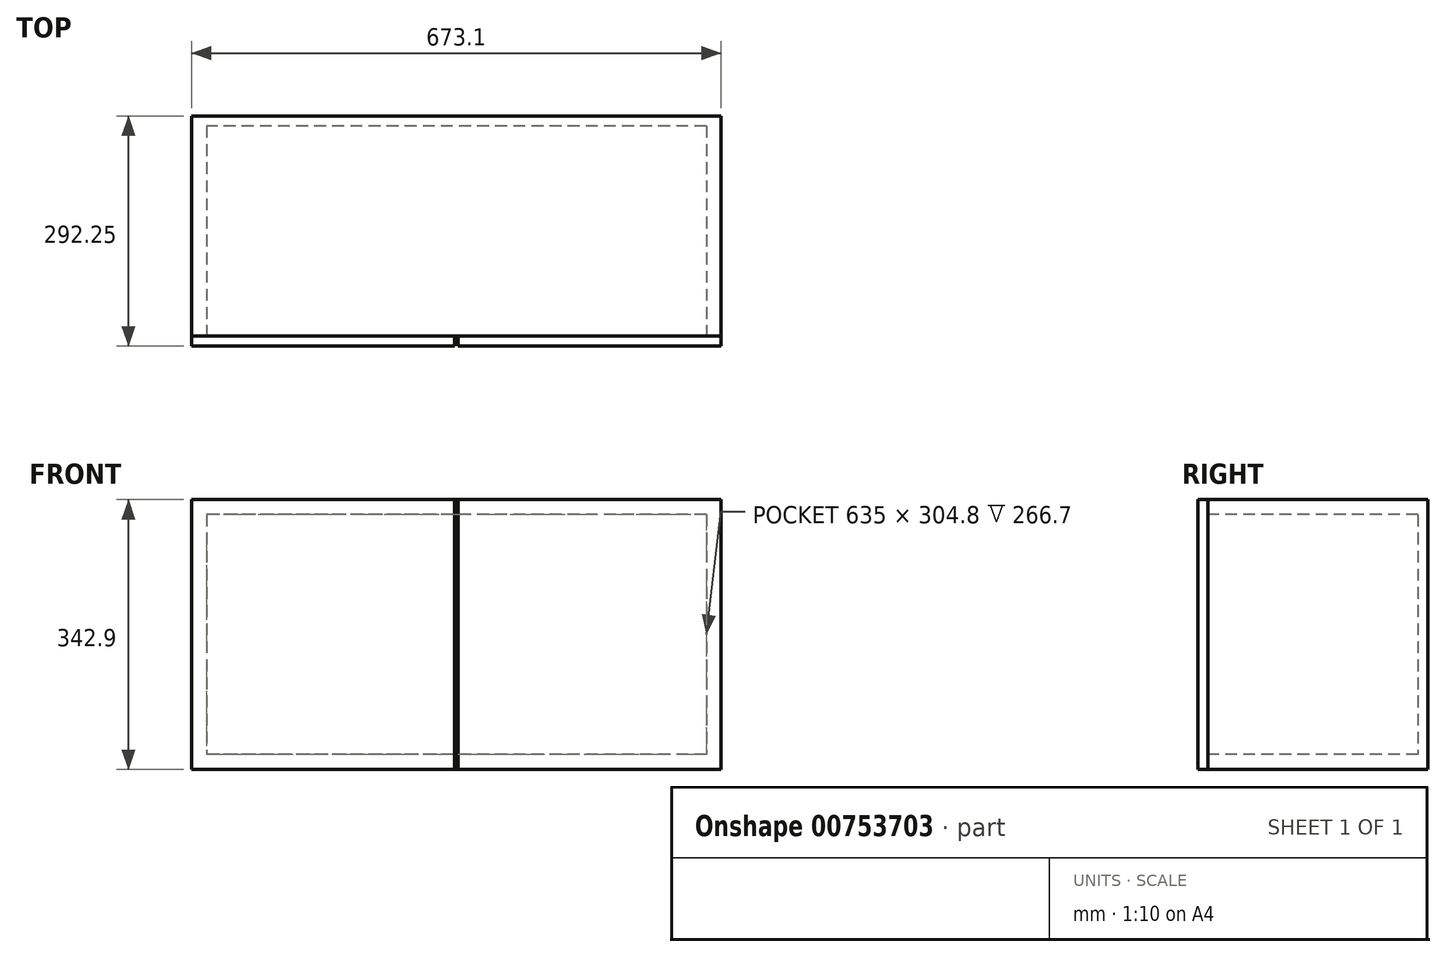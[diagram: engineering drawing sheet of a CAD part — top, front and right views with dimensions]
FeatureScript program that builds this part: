
annotation { "Feature Type Name" : "Feature", "Feature Type Description" : "" }
export const myFeature = defineFeature(function(context is Context, id is Id, definition is map)
    precondition{}
    {
        {
            var Q0;
            Q0=qCreatedBy(makeId("Front.planeOp"),FACE);
            var sketch = newSketch(context, id + "F0", { "sketchPlane" : qUnion([Q0])});
            skLineSegment(sketch, "E0.bottom", {"start": v(-336.55, 171.45) * mm, "end": v(336.55, 171.45) * mm});
            skLineSegment(sketch, "E0.top", {"start": v(-336.55, -171.45) * mm, "end": v(336.55, -171.45) * mm});
            skLineSegment(sketch, "E0.left", {"start": v(-336.55, 171.45) * mm, "end": v(-336.55, -171.45) * mm});
            skLineSegment(sketch, "E0.right", {"start": v(336.55, 171.45) * mm, "end": v(336.55, -171.45) * mm});
            skPoint(sketch, "E0.middle", {"position": v(0, 0) * mm});
            skSolve(sketch);
        }
        {
            var Q0;
            Q0=makeQuery(id+"F0.imprint","IMPRINT",FACE,{"disambiguationData":[TD([[makeQuery(id+"F0.imprint","IMPRINT",EDGE,{"derivedFrom":sQuery(id+"F0.wireOp",EDGE,"E0.bottom")}),-1.0]])]});
            extrude(context, id + "F1", {"entities" : qUnion([Q0]), "endBound" : BoundingType.SYMMETRIC, "depth" : 279.4 * mm, "offsetDistance" : 25 * mm});
        }
        {
            var Q0;
            Q0=makeQuery(id+"F1.opExtrude","CAP_FACE",FACE,{"disambiguationData":[OSD([sQuery(id+"F0.wireOp",EDGE,"E0.bottom"),sQuery(id+"F0.wireOp",EDGE,"E0.top"),sQuery(id+"F0.wireOp",EDGE,"E0.left"),sQuery(id+"F0.wireOp",EDGE,"E0.right")])],"isStart":false});
            var sketch = newSketch(context, id + "F2", { "sketchPlane" : qUnion([Q0])});
            skLineSegment(sketch, "E1.bottom", {"start": v(317.5, 152.4) * mm, "end": v(-317.5, 152.4) * mm});
            skLineSegment(sketch, "E1.top", {"start": v(317.5, -152.4) * mm, "end": v(-317.5, -152.4) * mm});
            skLineSegment(sketch, "E1.left", {"start": v(317.5, 152.4) * mm, "end": v(317.5, -152.4) * mm});
            skLineSegment(sketch, "E1.right", {"start": v(-317.5, 152.4) * mm, "end": v(-317.5, -152.4) * mm});
            skPoint(sketch, "E1.middle", {"position": v(0, 0) * mm});
            skSolve(sketch);
        }
        {
            var Q0;
            Q0=qSketchRegion(id+"F2",true);
            var Q1;
            Q1=makeQuery(id+"F1.opExtrude","CAP_FACE",FACE,{"disambiguationData":[OSD([sQuery(id+"F0.wireOp",EDGE,"E0.bottom"),sQuery(id+"F0.wireOp",EDGE,"E0.top"),sQuery(id+"F0.wireOp",EDGE,"E0.left"),sQuery(id+"F0.wireOp",EDGE,"E0.right")])],"isStart":true});
            extrude(context, id + "F3", {"entities" : qUnion([Q0]), "operationType" : NewBodyOperationType.REMOVE, "oppositeDirection" : true, "endBoundEntityFace" : qUnion([Q1]), "depth" : 266.7 * mm});
        }
        {
            var Q0;
            Q0=makeQuery(id+"F1.opExtrude","CAP_FACE",FACE,{"disambiguationData":[OSD([sQuery(id+"F0.wireOp",EDGE,"E0.bottom"),sQuery(id+"F0.wireOp",EDGE,"E0.top"),sQuery(id+"F0.wireOp",EDGE,"E0.left"),sQuery(id+"F0.wireOp",EDGE,"E0.right")])],"isStart":false});
            cPlane(context, id + "F4", {"entities" : qUnion([Q0]), "cplaneType" : CPlaneType.OFFSET, "offset" : .15 * mm, "width" : 150 * mm, "height" : 150 * mm});
        }
        {
            var Q0;
            Q0=qCreatedBy(id+"F4.planeOp",FACE);
            var sketch = newSketch(context, id + "F5", { "sketchPlane" : qUnion([Q0])});
            skLineSegment(sketch, "E2.bottom", {"start": v(-336.55, -171.45) * mm, "end": v(-1.9, -171.45) * mm});
            skLineSegment(sketch, "E2.top", {"start": v(-336.55, 171.45) * mm, "end": v(-1.9, 171.45) * mm});
            skLineSegment(sketch, "E2.left", {"start": v(-336.55, -171.45) * mm, "end": v(-336.55, 171.45) * mm});
            skLineSegment(sketch, "E2.right", {"start": v(-1.9, -171.45) * mm, "end": v(-1.9, 171.45) * mm});
            skSolve(sketch);
        }
        {
            var Q0;
            Q0=makeQuery(id+"F5.imprint","IMPRINT",FACE,{"disambiguationData":[TD([[makeQuery(id+"F5.imprint","IMPRINT",EDGE,{"derivedFrom":sQuery(id+"F5.wireOp",EDGE,"E2.bottom")}),1.0]])]});
            extrude(context, id + "F6", {"entities" : qUnion([Q0]), "depth" : 12.7 * mm});
        }
        {
            var Q0;
            Q0=makeQuery(id+"F6.opExtrude","SWEPT_BODY",BODY,{"disambiguationData":[OSD([sQuery(id+"F5.wireOp",EDGE,"E2.bottom"),sQuery(id+"F5.wireOp",EDGE,"E2.top"),sQuery(id+"F5.wireOp",EDGE,"E2.left"),sQuery(id+"F5.wireOp",EDGE,"E2.right")])]});
            var Q1;
            Q1=qCreatedBy(makeId("Right.planeOp"),FACE);
            mirror(context, id + "F7", {"entities" : qUnion([Q0]), "mirrorPlane" : qUnion([Q1])});
        }
    });
